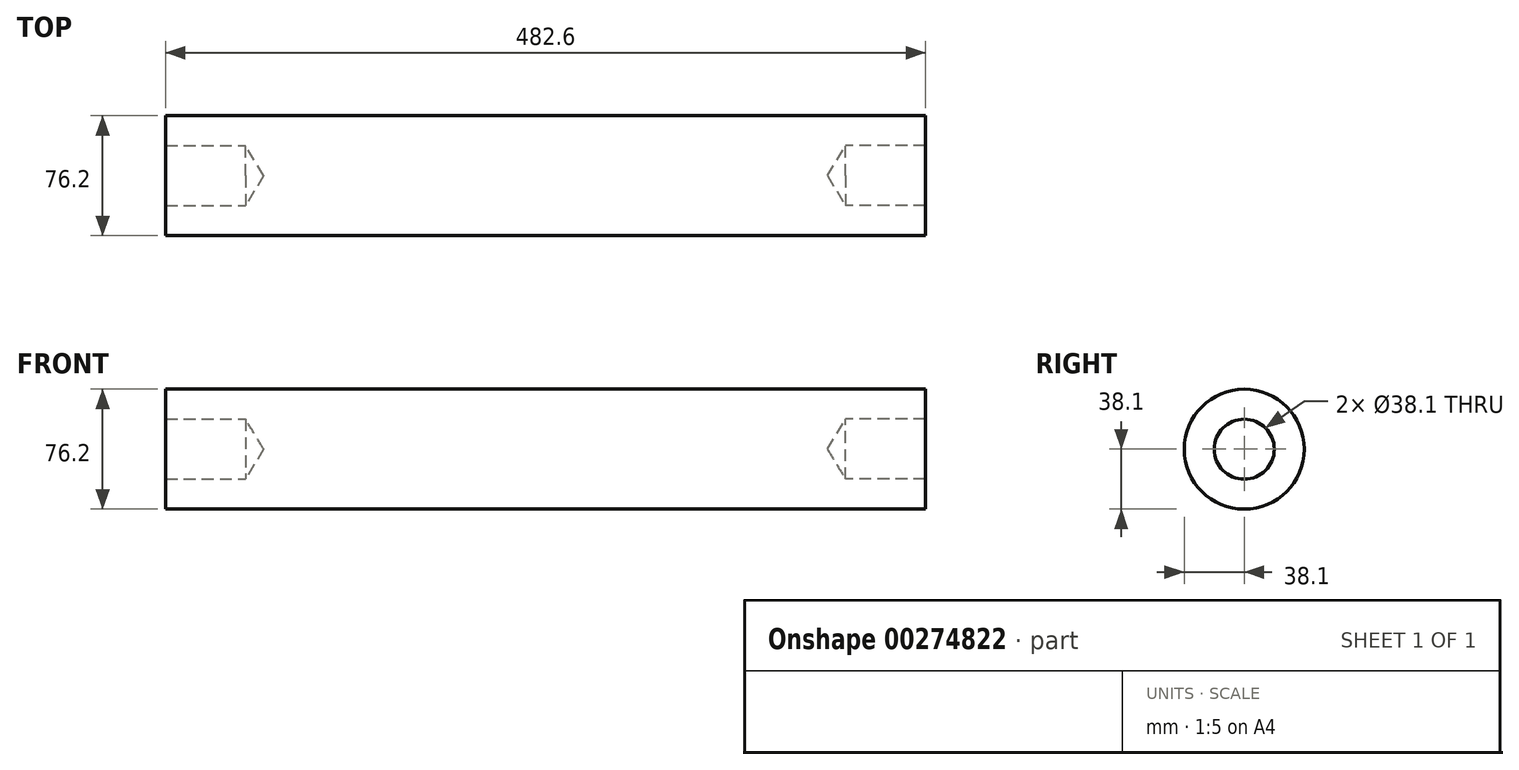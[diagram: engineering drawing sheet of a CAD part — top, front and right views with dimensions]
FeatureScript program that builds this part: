
annotation { "Feature Type Name" : "Feature", "Feature Type Description" : "" }
export const myFeature = defineFeature(function(context is Context, id is Id, definition is map)
    precondition{}
    {
        {
            var Q0;
            Q0=qCreatedBy(makeId("Right.planeOp"),FACE);
            var sketch = newSketch(context, id + "F0", { "sketchPlane" : qUnion([Q0])});
            skCircle(sketch, "E0", {"center": v(0, 0) * mm, "radius": 38.1 * mm});
            skSolve(sketch);
        }
        {
            var Q0;
            Q0=makeQuery(id+"F0.imprint","IMPRINT",FACE,{"disambiguationData":[TD([[makeQuery(id+"F0.imprint","IMPRINT",EDGE,{"derivedFrom":sQuery(id+"F0.wireOp",EDGE,"E0")}),1.0]])]});
            extrude(context, id + "F1", {"entities" : qUnion([Q0]), "depth" : 482.6 * mm, "symmetric" : true});
        }
        {
            var Q0;
            Q0=makeQuery(id+"F1.opExtrude","CAP_FACE",FACE,{"disambiguationData":[OSD([sQuery(id+"F0.wireOp",EDGE,"E0")])],"isStart":true});
            var sketch = newSketch(context, id + "F2", { "sketchPlane" : qUnion([Q0])});
            skPoint(sketch, "E1", {"position": v(0, 0) * mm});
            skSolve(sketch);
        }
        {
            var Q0;
            Q0=sQuery(id+"F2.wireOp",VERTEX,"E1");
            var Q1;
            Q1=makeQuery(id+"F1.opExtrude","SWEPT_BODY",BODY,{"disambiguationData":[OSD([sQuery(id+"F0.wireOp",EDGE,"E0")])]});
            hole(context, id + "F3", {"style" : HoleStyle.SIMPLE, "endStyle" : HoleEndStyle.BLIND, "holeDiameter" : 38.1 * mm, "holeDepth" : 50.8 * mm, "tappedDepth" : 12.7 * mm, "tapClearance" : 3, "locations" : qUnion([Q0]), "scope" : qUnion([Q1])});
        }
        {
            var Q0;
            Q0=makeQuery(id+"F1.opExtrude","CAP_FACE",FACE,{"disambiguationData":[OSD([sQuery(id+"F0.wireOp",EDGE,"E0")])],"isStart":false});
            var sketch = newSketch(context, id + "F4", { "sketchPlane" : qUnion([Q0])});
            skPoint(sketch, "E2", {"position": v(0, 0) * mm});
            skSolve(sketch);
        }
        {
            var Q0;
            Q0=sQuery(id+"F4.wireOp",VERTEX,"E2");
            var Q1;
            Q1=makeQuery(id+"F1.opExtrude","SWEPT_BODY",BODY,{"disambiguationData":[OSD([sQuery(id+"F0.wireOp",EDGE,"E0")])]});
            hole(context, id + "F5", {"style" : HoleStyle.SIMPLE, "endStyle" : HoleEndStyle.BLIND, "holeDiameter" : 38.1 * mm, "holeDepth" : 50.8 * mm, "tappedDepth" : 12.7 * mm, "tapClearance" : 3, "locations" : qUnion([Q0]), "scope" : qUnion([Q1])});
        }
    });
